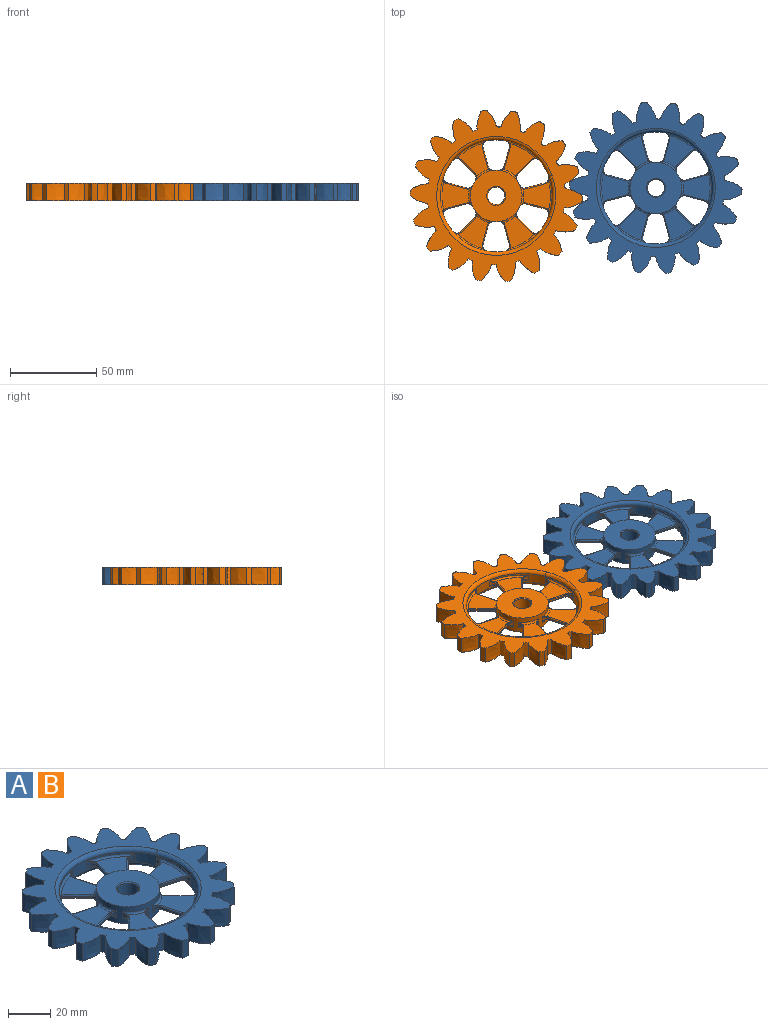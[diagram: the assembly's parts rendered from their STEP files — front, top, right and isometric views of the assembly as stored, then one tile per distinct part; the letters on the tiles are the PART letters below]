
ASSEMBLY  parts=2 mates=1
PART A: 303 faces, bbox 100x99.4x10 mm
  f0: plane 8.2x8.2mm, normal (0.71,-0.71,0), area 11.6mm2, adj f1,f5,f163,f208
  f1: cylinder r=3mm len=4mm, axis (0,0,1), area 8.2mm2, adj f0,f115,f161,f162,f209,f210
  f2: cylinder r=3mm len=4mm, axis (0,0,1), area 8.2mm2, adj f3,f115,f171,f172,f224,f225
  f3: plane 11.2x3mm, normal (-0.26,0.97,0), area 11.6mm2, adj f2,f4,f173,f223
  f4: cylinder r=3mm len=4mm, axis (0,0,1), area 9.6mm2, adj f3,f116,f174,f175,f221,f222
  f5: cylinder r=3mm len=4.45mm, axis (0,0,1), area 9.6mm2, adj f0,f116,f164,f165,f206,f207
  f6: plane 11.2x3mm, normal (-0.26,-0.97,0), area 11.6mm2, adj f7,f11,f168,f218
  f7: cylinder r=3mm len=4mm, axis (0,0,1), area 8.2mm2, adj f6,f115,f166,f167,f219,f220
  f8: cylinder r=3mm len=4mm, axis (0,0,1), area 8.2mm2, adj f9,f115,f256,f257,f269,f270
  f9: plane 8.2x8.2mm, normal (0.71,0.71,0), area 11.6mm2, adj f8,f10,f258,f268
  f10: cylinder r=3mm len=4.45mm, axis (0,0,1), area 9.6mm2, adj f9,f116,f259,f260,f266,f267
  f11: cylinder r=3mm len=4mm, axis (0,0,1), area 9.6mm2, adj f6,f116,f169,f170,f216,f217
  f12: plane 11.2x3mm, normal (-0.97,-0.26,0), area 11.6mm2, adj f13,f17,f263,f273
  f13: cylinder r=3mm len=4mm, axis (0,0,1), area 8.2mm2, adj f12,f115,f264,f265,f271,f272
  f14: cylinder r=3mm len=4mm, axis (0,0,1), area 8.2mm2, adj f15,f115,f181,f182,f254,f255
  f15: plane 11.2x3mm, normal (0.97,-0.26,0), area 11.6mm2, adj f14,f16,f183,f253
  f16: cylinder r=3mm len=4mm, axis (0,0,1), area 9.6mm2, adj f15,f116,f184,f185,f251,f252
  f17: cylinder r=3mm len=4mm, axis (0,0,1), area 9.6mm2, adj f12,f116,f261,f262,f274,f275
  f18: plane 8.2x8.2mm, normal (-0.71,0.71,0), area 11.6mm2, adj f19,f23,f203,f248
  f19: cylinder r=3mm len=4mm, axis (0,0,1), area 8.2mm2, adj f18,f115,f204,f205,f249,f250
  f20: cylinder r=3mm len=4mm, axis (0,0,1), area 8.2mm2, adj f21,f115,f199,f200,f244,f245
  f21: plane 11.2x3mm, normal (0.26,-0.97,0), area 11.6mm2, adj f20,f22,f198,f243
  f22: cylinder r=3mm len=4mm, axis (0,0,1), area 9.6mm2, adj f21,f116,f196,f197,f241,f242
  f23: cylinder r=3mm len=4.45mm, axis (0,0,1), area 9.6mm2, adj f18,f116,f201,f202,f246,f247
  f24: plane 11.2x3mm, normal (0.26,0.97,0), area 11.6mm2, adj f25,f29,f193,f238
  f25: cylinder r=3mm len=4mm, axis (0,0,1), area 8.2mm2, adj f24,f115,f194,f195,f239,f240
  f26: cylinder r=3mm len=4mm, axis (0,0,1), area 8.2mm2, adj f27,f115,f189,f190,f234,f235
  f27: plane 8.2x8.2mm, normal (-0.71,-0.71,0), area 11.6mm2, adj f26,f28,f188,f233
  f28: cylinder r=3mm len=4.45mm, axis (0,0,1), area 9.6mm2, adj f27,f116,f186,f187,f231,f232
  f29: cylinder r=3mm len=4mm, axis (0,0,1), area 9.6mm2, adj f24,f116,f191,f192,f236,f237
  f30: plane 11.2x3mm, normal (0.97,0.26,0), area 11.6mm2, adj f31,f35,f178,f228
  f31: cylinder r=3mm len=4mm, axis (0,0,1), area 8.2mm2, adj f30,f115,f176,f177,f229,f230
  f32: cylinder r=3mm len=4mm, axis (0,0,1), area 8.2mm2, adj f33,f115,f214,f215,f279,f280
  f33: plane 11.2x3mm, normal (-0.97,0.26,0), area 11.6mm2, adj f32,f34,f213,f278
  f34: cylinder r=3mm len=4mm, axis (0,0,1), area 9.6mm2, adj f33,f116,f211,f212,f276,f277
  f35: cylinder r=3mm len=4mm, axis (0,0,1), area 9.6mm2, adj f30,f116,f179,f180,f226,f227
  f36: plane 30x30mm, normal (0,0,-1), area 611.8mm2, adj f113,f115,f132
  f37: plane 99.99x99.35mm, normal (0,0,-1), area 2808.6mm2, adj f40,f41,f42,f43,f44,f45,f46,f47
  f38: plane 30x30mm, normal (0,0,1), area 611.8mm2, adj f114,f115,f124
  f39: plane 99.99x99.35mm, normal (0,0,1), area 2808.6mm2, adj f40,f41,f42,f43,f44,f45,f46,f47
  f40: cylinder r=50mm len=10mm, axis (0,0,-1), area 32.4mm2, adj f37,f39,f63,f109
  f41: cylinder r=50mm len=10mm, axis (0,0,-1), area 32.4mm2, adj f37,f39,f66,f106
  f42: cylinder r=50mm len=10mm, axis (0,0,-1), area 32.4mm2, adj f37,f39,f102,f103
  f43: cylinder r=50mm len=10mm, axis (0,0,-1), area 32.4mm2, adj f37,f39,f100,f108
  f44: cylinder r=50mm len=10mm, axis (0,0,-1), area 32.4mm2, adj f37,f39,f97,f111
  f45: cylinder r=50mm len=10mm, axis (0,0,-1), area 32.4mm2, adj f37,f39,f94,f99
  f46: cylinder r=50mm len=10mm, axis (0,0,-1), area 17.2mm2, adj f37,f39,f298,f302
  f47: cylinder r=50mm len=10mm, axis (0,0,-1), area 17.2mm2, adj f37,f39,f281,f299
  f48: cylinder r=50mm len=10mm, axis (0,0,-1), area 17.2mm2, adj f37,f39,f294,f296
  f49: cylinder r=50mm len=10mm, axis (0,0,-1), area 17.2mm2, adj f37,f39,f286,f288
  f50: cylinder r=50mm len=10mm, axis (0,0,-1), area 17.2mm2, adj f37,f39,f282,f284
  f51: cylinder r=50mm len=10mm, axis (0,0,-1), area 32.4mm2, adj f37,f39,f75,f76
  f52: cylinder r=50mm len=10mm, axis (0,0,-1), area 32.4mm2, adj f37,f39,f73,f81
  f53: cylinder r=50mm len=10mm, axis (0,0,-1), area 32.4mm2, adj f37,f39,f70,f78
  f54: cylinder r=50mm len=10mm, axis (0,0,-1), area 32.4mm2, adj f37,f39,f67,f72
  f55: cylinder r=50mm len=10mm, axis (0,0,-1), area 32.4mm2, adj f37,f39,f64,f69
  f56: cylinder r=50mm len=10mm, axis (0,0,-1), area 32.4mm2, adj f37,f39,f61,f105
  f57: cylinder r=50mm len=10mm, axis (0,0,-1), area 17.2mm2, adj f37,f39,f290,f292
  f58: extruded ~10x8.03mm, area 93.6mm2, adj f37,f39,f289,f290
  f59: cylinder r=40mm len=10mm, axis (0,0,1), area 3.4mm2, adj f37,f39,f287,f289
  f60: extruded ~10x9.25mm, area 93.6mm2, adj f37,f39,f287,f288
  f61: extruded ~10.49x10mm, area 112.7mm2, adj f37,f39,f56,f62
  f62: cylinder r=40mm len=10mm, axis (0,0,1), area 27.9mm2, adj f37,f39,f61,f63
  f63: extruded ~10x8.13mm, area 112.7mm2, adj f37,f39,f40,f62
  f64: extruded ~10.96x10mm, area 112.7mm2, adj f37,f39,f55,f65
  f65: cylinder r=40mm len=10mm, axis (0,0,1), area 27.9mm2, adj f37,f39,f64,f66
  f66: extruded ~10x8.84mm, area 112.7mm2, adj f37,f39,f41,f65
  f67: extruded ~10x9.71mm, area 112.7mm2, adj f37,f39,f54,f68
  f68: cylinder r=40mm len=10mm, axis (0,0,1), area 27.9mm2, adj f37,f39,f67,f69
  f69: extruded ~10x9.32mm, area 112.7mm2, adj f37,f39,f55,f68
  f70: extruded ~10x8.35mm, area 112.7mm2, adj f37,f39,f53,f71
  f71: cylinder r=40mm len=10mm, axis (0,0,1), area 27.9mm2, adj f37,f39,f70,f72
  f72: extruded ~10.81x10mm, area 112.7mm2, adj f37,f39,f54,f71
  f73: extruded ~11.09x10mm, area 112.7mm2, adj f37,f39,f52,f74
  f74: cylinder r=40mm len=10mm, axis (0,0,1), area 27.9mm2, adj f37,f39,f73,f75
  f75: extruded ~10x9.87mm, area 112.7mm2, adj f37,f39,f51,f74
  f76: extruded ~10.34x10mm, area 112.7mm2, adj f37,f39,f51,f77
  f77: cylinder r=40mm len=10mm, axis (0,0,1), area 27.9mm2, adj f37,f39,f76,f78
  f78: extruded ~11x10mm, area 112.7mm2, adj f37,f39,f53,f77
  f79: extruded ~10x9.85mm, area 105mm2, adj f37,f39,f80,f282
  f80: cylinder r=40mm len=10mm, axis (0,0,1), area 27.9mm2, adj f37,f39,f79,f81
  f81: extruded ~10x8.13mm, area 112.7mm2, adj f37,f39,f52,f80
  f82: extruded ~10x7.1mm, area 93.6mm2, adj f37,f39,f285,f286
  f83: cylinder r=40mm len=10mm, axis (0,0,1), area 3.4mm2, adj f37,f39,f283,f285
  f84: extruded ~10x8.47mm, area 93.6mm2, adj f37,f39,f283,f284
  f85: extruded ~10x9.13mm, area 93.6mm2, adj f37,f39,f293,f294
  f86: cylinder r=40mm len=10mm, axis (0,0,1), area 3.4mm2, adj f37,f39,f291,f293
  f87: extruded ~10x8.92mm, area 93.6mm2, adj f37,f39,f291,f292
  f88: extruded ~10x8.03mm, area 93.6mm2, adj f37,f39,f299,f300
  f89: cylinder r=40mm len=10mm, axis (0,0,1), area 3.4mm2, adj f37,f39,f300,f301
  f90: extruded ~10x7.69mm, area 93.6mm2, adj f37,f39,f301,f302
  f91: extruded ~10x9.13mm, area 93.6mm2, adj f37,f39,f297,f298
  f92: cylinder r=40mm len=10mm, axis (0,0,1), area 3.4mm2, adj f37,f39,f295,f297
  f93: extruded ~10x7.5mm, area 93.6mm2, adj f37,f39,f295,f296
  f94: extruded ~10x8.35mm, area 112.7mm2, adj f37,f39,f45,f95
  f95: cylinder r=40mm len=10mm, axis (0,0,1), area 27.9mm2, adj f37,f39,f94,f96
  f96: extruded ~10.13x10mm, area 105mm2, adj f37,f39,f95,f281
  f97: extruded ~10.34x10mm, area 112.7mm2, adj f37,f39,f44,f98
  f98: cylinder r=40mm len=10mm, axis (0,0,1), area 27.9mm2, adj f37,f39,f97,f99
  f99: extruded ~11x10mm, area 112.7mm2, adj f37,f39,f45,f98
  f100: extruded ~10x9.49mm, area 112.7mm2, adj f37,f39,f43,f101
  f101: cylinder r=40mm len=10mm, axis (0,0,1), area 27.9mm2, adj f37,f39,f100,f102
  f102: extruded ~11.08x10mm, area 112.7mm2, adj f37,f39,f42,f101
  f103: extruded ~10x8.64mm, area 112.7mm2, adj f37,f39,f42,f104
  f104: cylinder r=40mm len=10mm, axis (0,0,1), area 27.9mm2, adj f37,f39,f103,f105
  f105: extruded ~10.22x10mm, area 112.7mm2, adj f37,f39,f56,f104
  f106: extruded ~10.88x10mm, area 112.7mm2, adj f37,f39,f41,f107
  f107: cylinder r=40mm len=10mm, axis (0,0,1), area 27.9mm2, adj f37,f39,f106,f108
  f108: extruded ~10.6x10mm, area 112.7mm2, adj f37,f39,f43,f107
  f109: extruded ~11.09x10mm, area 112.7mm2, adj f37,f39,f40,f110
  f110: cylinder r=40mm len=10mm, axis (0,0,1), area 27.9mm2, adj f37,f39,f109,f111
  f111: extruded ~10x9.87mm, area 112.7mm2, adj f37,f39,f44,f110
  f112: cylinder r=5mm len=10mm, axis (0,0,1), area 282.7mm2, adj f113,f114
  f113: cone r=5.5mm half-angle=45deg, axis (0,0,-1), area 23.3mm2, adj f36,f112
  f114: cone r=5mm half-angle=45deg, axis (0,0,1), area 23.3mm2, adj f38,f112
  f115: cylinder r=15mm len=30mm, axis (0,0,1), area 556.2mm2, adj f1,f2,f7,f8,f13,f14,f19,f20
  f116: cylinder r=32.5mm len=65mm, axis (0,0,1), area 610.6mm2, adj f4,f5,f10,f11,f16,f17,f22,f23
  f117: plane 19.15x18.27mm, normal (0,0,1), area 178.8mm2, adj f152,f156,f177,f178,f179,f187,f188,f189
  f118: plane 19.15x18.27mm, normal (0,0,1), area 178.8mm2, adj f159,f160,f162,f163,f164,f277,f278,f279
  f119: plane 16.77x16.04mm, normal (0,0,1), area 178.8mm2, adj f151,f155,f192,f193,f194,f197,f198,f199
  f120: plane 19.15x18.27mm, normal (0,0,1), area 178.8mm2, adj f150,f154,f182,f183,f184,f202,f203,f204
  f121: plane 19.15x18.27mm, normal (0,0,1), area 178.8mm2, adj f149,f153,f267,f268,f269,f272,f273,f274
  f122: plane 16.78x16.04mm, normal (0,0,1), area 178.8mm2, adj f157,f158,f167,f168,f169,f172,f173,f174
  f123: extruded ~23.12x2.13mm, area 23.6mm2, adj f116,f136,f157
  f124: extruded ~12.49x3mm, area 38.6mm2, adj f38,f115,f158
  f125: plane 19.15x18.27mm, normal (0,0,-1), area 178.8mm2, adj f140,f144,f227,f228,f229,f232,f233,f234
  f126: plane 19.15x18.27mm, normal (0,0,-1), area 178.8mm2, adj f147,f148,f207,f208,f209,f212,f213,f214
  f127: plane 16.77x16.04mm, normal (0,0,-1), area 178.8mm2, adj f139,f143,f237,f238,f239,f242,f243,f244
  f128: plane 19.15x18.27mm, normal (0,0,-1), area 178.8mm2, adj f138,f142,f247,f248,f249,f252,f253,f254
  f129: plane 19.15x18.27mm, normal (0,0,-1), area 178.8mm2, adj f137,f141,f257,f258,f259,f262,f263,f264
  f130: plane 16.78x16.04mm, normal (0,0,-1), area 178.8mm2, adj f145,f146,f217,f218,f219,f222,f223,f224
  f131: extruded ~23.12x2.13mm, area 23.6mm2, adj f116,f134,f145
  f132: extruded ~12.49x3mm, area 38.6mm2, adj f36,f115,f146
  f133: torus R=34.5mm, axis (0,0,1), area 579.9mm2, adj f37,f116,f134
  f134: bspline ~32.37x5.62mm, area 75.9mm2, adj f37,f131,f133
  f135: torus R=34.5mm, axis (0,0,1), area 579.9mm2, adj f39,f116,f136
  f136: bspline ~32.37x5.62mm, area 75.9mm2, adj f39,f123,f135
  f137: torus R=31.5mm, axis (0,0,-1), area 32mm2, adj f116,f129,f260,f261
  f138: torus R=31.5mm, axis (0,0,-1), area 32mm2, adj f116,f128,f246,f251
  f139: torus R=31.5mm, axis (0,0,-1), area 32mm2, adj f116,f127,f236,f241
  f140: torus R=31.5mm, axis (0,0,-1), area 32mm2, adj f116,f125,f226,f231
  f141: torus R=16mm, axis (0,0,-1), area 16.6mm2, adj f115,f129,f256,f265
  f142: torus R=16mm, axis (0,0,-1), area 16.6mm2, adj f115,f128,f250,f255
  f143: torus R=16mm, axis (0,0,-1), area 16.6mm2, adj f115,f127,f240,f245
  f144: torus R=16mm, axis (0,0,-1), area 16.6mm2, adj f115,f125,f230,f235
  f145: bspline ~27.91x4.74mm, area 32mm2, adj f130,f131,f216,f221
  f146: bspline ~13.79x2.51mm, area 16.6mm2, adj f130,f132,f220,f225
  f147: torus R=16mm, axis (0,0,-1), area 16.6mm2, adj f115,f126,f210,f215
  f148: torus R=31.5mm, axis (0,0,-1), area 32mm2, adj f116,f126,f206,f211
  f149: torus R=31.5mm, axis (0,0,1), area 32mm2, adj f116,f121,f266,f275
  f150: torus R=31.5mm, axis (0,0,1), area 32mm2, adj f116,f120,f185,f201
  f151: torus R=31.5mm, axis (0,0,1), area 32mm2, adj f116,f119,f191,f196
  f152: torus R=31.5mm, axis (0,0,1), area 32mm2, adj f116,f117,f180,f186
  f153: torus R=16mm, axis (0,0,1), area 16.6mm2, adj f115,f121,f270,f271
  f154: torus R=16mm, axis (0,0,1), area 16.6mm2, adj f115,f120,f181,f205
  f155: torus R=16mm, axis (0,0,1), area 16.6mm2, adj f115,f119,f195,f200
  f156: torus R=16mm, axis (0,0,1), area 16.6mm2, adj f115,f117,f176,f190
  f157: bspline ~27.91x4.74mm, area 32mm2, adj f122,f123,f170,f175
  f158: bspline ~14.11x2.58mm, area 16.6mm2, adj f122,f124,f166,f171
  f159: torus R=16mm, axis (0,0,1), area 16.6mm2, adj f115,f118,f161,f280
  f160: torus R=31.5mm, axis (0,0,1), area 32mm2, adj f116,f118,f165,f276
  f161: bspline ~2.9x1.5mm, area 0.8mm2, adj f1,f159,f162
  f162: torus R=3.5mm, axis (0,0,1), area 1.3mm2, adj f1,f118,f161,f163
  f163: cylinder r=0.5mm len=8.56mm, axis (-0.71,-0.71,0), area 9.1mm2, adj f0,f118,f162,f164
  f164: torus R=3.5mm, axis (0,0,1), area 1.7mm2, adj f5,f118,f163,f165
  f165: bspline ~3.06x1.59mm, area 0.9mm2, adj f5,f160,f164
  f166: bspline ~2.24x2.23mm, area 0.8mm2, adj f7,f158,f167
  f167: torus R=3.5mm, axis (0,0,1), area 1.3mm2, adj f7,f122,f166,f168
  f168: cylinder r=0.5mm len=11.33mm, axis (-0.97,0.26,0), area 9.1mm2, adj f6,f122,f167,f169
  f169: torus R=3.5mm, axis (0,0,1), area 1.7mm2, adj f11,f122,f168,f170
  f170: bspline ~3.44x1.5mm, area 0.9mm2, adj f11,f157,f169
  f171: bspline ~2.24x2.23mm, area 0.8mm2, adj f2,f158,f172
  f172: torus R=3.5mm, axis (0,0,1), area 1.3mm2, adj f2,f122,f171,f173
  f173: cylinder r=0.5mm len=11.33mm, axis (0.97,0.26,0), area 9.1mm2, adj f3,f122,f172,f174
  f174: torus R=3.5mm, axis (0,0,1), area 1.7mm2, adj f4,f122,f173,f175
  f175: bspline ~3.44x1.5mm, area 0.9mm2, adj f4,f157,f174
  f176: bspline ~2.96x1.5mm, area 0.8mm2, adj f31,f156,f177
  f177: torus R=3.5mm, axis (0,0,1), area 1.3mm2, adj f31,f117,f176,f178
  f178: cylinder r=0.5mm len=11.33mm, axis (0.26,-0.97,0), area 9.1mm2, adj f30,f117,f177,f179
  f179: torus R=3.5mm, axis (0,0,1), area 1.7mm2, adj f35,f117,f178,f180
  f180: bspline ~2.75x1.79mm, area 0.9mm2, adj f35,f152,f179
  f181: bspline ~2.96x1.5mm, area 0.8mm2, adj f14,f154,f182
  f182: torus R=3.5mm, axis (0,0,1), area 1.3mm2, adj f14,f120,f181,f183
  f183: cylinder r=0.5mm len=11.33mm, axis (-0.26,-0.97,0), area 9.1mm2, adj f15,f120,f182,f184
  f184: torus R=3.5mm, axis (0,0,1), area 1.7mm2, adj f16,f120,f183,f185
  f185: bspline ~2.9x2.1mm, area 0.9mm2, adj f16,f150,f184
  f186: bspline ~3.06x1.59mm, area 0.9mm2, adj f28,f152,f187
  f187: torus R=3.5mm, axis (0,0,1), area 1.7mm2, adj f28,f117,f186,f188
  f188: cylinder r=0.5mm len=8.56mm, axis (-0.71,0.71,0), area 9.1mm2, adj f27,f117,f187,f189
  f189: torus R=3.5mm, axis (0,0,1), area 1.3mm2, adj f26,f117,f188,f190
  f190: bspline ~2.9x1.5mm, area 0.8mm2, adj f26,f156,f189
  f191: bspline ~3.44x1.5mm, area 0.9mm2, adj f29,f151,f192
  f192: torus R=3.5mm, axis (0,0,1), area 1.7mm2, adj f29,f119,f191,f193
  f193: cylinder r=0.5mm len=11.33mm, axis (0.97,-0.26,0), area 9.1mm2, adj f24,f119,f192,f194
  f194: torus R=3.5mm, axis (0,0,1), area 1.3mm2, adj f25,f119,f193,f195
  f195: bspline ~2.24x2.23mm, area 0.8mm2, adj f25,f155,f194
  f196: bspline ~3.44x1.5mm, area 0.9mm2, adj f22,f151,f197
  f197: torus R=3.5mm, axis (0,0,1), area 1.7mm2, adj f22,f119,f196,f198
  f198: cylinder r=0.5mm len=11.33mm, axis (-0.97,-0.26,0), area 9.1mm2, adj f21,f119,f197,f199
  f199: torus R=3.5mm, axis (0,0,1), area 1.3mm2, adj f20,f119,f198,f200
  f200: bspline ~2.24x2.23mm, area 0.8mm2, adj f20,f155,f199
  f201: bspline ~3.06x1.59mm, area 0.9mm2, adj f23,f150,f202
  f202: torus R=3.5mm, axis (0,0,1), area 1.7mm2, adj f23,f120,f201,f203
  f203: cylinder r=0.5mm len=8.56mm, axis (0.71,0.71,0), area 9.1mm2, adj f18,f120,f202,f204
  f204: torus R=3.5mm, axis (0,0,1), area 1.3mm2, adj f19,f120,f203,f205
  f205: bspline ~2.9x1.5mm, area 0.8mm2, adj f19,f154,f204
  f206: bspline ~3.06x1.59mm, area 0.9mm2, adj f5,f148,f207
  f207: torus R=3.5mm, axis (0,0,-1), area 1.7mm2, adj f5,f126,f206,f208
  f208: cylinder r=0.5mm len=8.56mm, axis (0.71,0.71,0), area 9.1mm2, adj f0,f126,f207,f209
  f209: torus R=3.5mm, axis (0,0,-1), area 1.3mm2, adj f1,f126,f208,f210
  f210: bspline ~2.9x1.5mm, area 0.8mm2, adj f1,f147,f209
  f211: bspline ~2.9x2.1mm, area 0.9mm2, adj f34,f148,f212
  f212: torus R=3.5mm, axis (0,0,-1), area 1.7mm2, adj f34,f126,f211,f213
  f213: cylinder r=0.5mm len=11.33mm, axis (-0.26,-0.97,0), area 9.1mm2, adj f33,f126,f212,f214
  f214: torus R=3.5mm, axis (0,0,-1), area 1.3mm2, adj f32,f126,f213,f215
  f215: bspline ~2.96x1.5mm, area 0.8mm2, adj f32,f147,f214
  f216: bspline ~3.44x1.5mm, area 0.9mm2, adj f11,f145,f217
  f217: torus R=3.5mm, axis (0,0,-1), area 1.7mm2, adj f11,f130,f216,f218
  f218: cylinder r=0.5mm len=11.33mm, axis (0.97,-0.26,0), area 9.1mm2, adj f6,f130,f217,f219
  f219: torus R=3.5mm, axis (0,0,-1), area 1.3mm2, adj f7,f130,f218,f220
  f220: bspline ~2.24x2.23mm, area 0.8mm2, adj f7,f146,f219
  f221: bspline ~3.44x1.5mm, area 0.9mm2, adj f4,f145,f222
  f222: torus R=3.5mm, axis (0,0,-1), area 1.7mm2, adj f4,f130,f221,f223
  f223: cylinder r=0.5mm len=11.33mm, axis (-0.97,-0.26,0), area 9.1mm2, adj f3,f130,f222,f224
  f224: torus R=3.5mm, axis (0,0,-1), area 1.3mm2, adj f2,f130,f223,f225
  f225: bspline ~2.24x2.23mm, area 0.8mm2, adj f2,f146,f224
  f226: bspline ~2.9x2.1mm, area 0.9mm2, adj f35,f140,f227
  f227: torus R=3.5mm, axis (0,0,-1), area 1.7mm2, adj f35,f125,f226,f228
  f228: cylinder r=0.5mm len=11.33mm, axis (-0.26,0.97,0), area 9.1mm2, adj f30,f125,f227,f229
  f229: torus R=3.5mm, axis (0,0,-1), area 1.3mm2, adj f31,f125,f228,f230
  f230: bspline ~2.96x1.5mm, area 0.8mm2, adj f31,f144,f229
  f231: bspline ~3.06x1.59mm, area 0.9mm2, adj f28,f140,f232
  f232: torus R=3.5mm, axis (0,0,-1), area 1.7mm2, adj f28,f125,f231,f233
  f233: cylinder r=0.5mm len=8.56mm, axis (0.71,-0.71,0), area 9.1mm2, adj f27,f125,f232,f234
  f234: torus R=3.5mm, axis (0,0,-1), area 1.3mm2, adj f26,f125,f233,f235
  f235: bspline ~2.9x1.5mm, area 0.8mm2, adj f26,f144,f234
  f236: bspline ~3.44x1.5mm, area 0.9mm2, adj f29,f139,f237
  f237: torus R=3.5mm, axis (0,0,-1), area 1.7mm2, adj f29,f127,f236,f238
  f238: cylinder r=0.5mm len=11.33mm, axis (-0.97,0.26,0), area 9.1mm2, adj f24,f127,f237,f239
  f239: torus R=3.5mm, axis (0,0,-1), area 1.3mm2, adj f25,f127,f238,f240
  f240: bspline ~2.24x2.23mm, area 0.8mm2, adj f25,f143,f239
  f241: bspline ~3.44x1.5mm, area 0.9mm2, adj f22,f139,f242
  f242: torus R=3.5mm, axis (0,0,-1), area 1.7mm2, adj f22,f127,f241,f243
  f243: cylinder r=0.5mm len=11.33mm, axis (0.97,0.26,0), area 9.1mm2, adj f21,f127,f242,f244
  f244: torus R=3.5mm, axis (0,0,-1), area 1.3mm2, adj f20,f127,f243,f245
  f245: bspline ~2.24x2.23mm, area 0.8mm2, adj f20,f143,f244
  f246: bspline ~3.06x1.59mm, area 0.9mm2, adj f23,f138,f247
  f247: torus R=3.5mm, axis (0,0,-1), area 1.7mm2, adj f23,f128,f246,f248
  f248: cylinder r=0.5mm len=8.56mm, axis (-0.71,-0.71,0), area 9.1mm2, adj f18,f128,f247,f249
  f249: torus R=3.5mm, axis (0,0,-1), area 1.3mm2, adj f19,f128,f248,f250
  f250: bspline ~2.9x1.5mm, area 0.8mm2, adj f19,f142,f249
  f251: bspline ~2.9x2.1mm, area 0.9mm2, adj f16,f138,f252
  f252: torus R=3.5mm, axis (0,0,-1), area 1.7mm2, adj f16,f128,f251,f253
  f253: cylinder r=0.5mm len=11.33mm, axis (0.26,0.97,0), area 9.1mm2, adj f15,f128,f252,f254
  f254: torus R=3.5mm, axis (0,0,-1), area 1.3mm2, adj f14,f128,f253,f255
  f255: bspline ~2.96x1.5mm, area 0.8mm2, adj f14,f142,f254
  f256: bspline ~2.9x1.5mm, area 0.8mm2, adj f8,f141,f257
  f257: torus R=3.5mm, axis (0,0,-1), area 1.3mm2, adj f8,f129,f256,f258
  f258: cylinder r=0.5mm len=8.56mm, axis (-0.71,0.71,0), area 9.1mm2, adj f9,f129,f257,f259
  f259: torus R=3.5mm, axis (0,0,-1), area 1.7mm2, adj f10,f129,f258,f260
  f260: bspline ~2.76x1.58mm, area 0.9mm2, adj f10,f137,f259
  f261: bspline ~2.9x2.1mm, area 0.9mm2, adj f17,f137,f262
  f262: torus R=3.5mm, axis (0,0,-1), area 1.7mm2, adj f17,f129,f261,f263
  f263: cylinder r=0.5mm len=11.33mm, axis (0.26,-0.97,0), area 9.1mm2, adj f12,f129,f262,f264
  f264: torus R=3.5mm, axis (0,0,-1), area 1.3mm2, adj f13,f129,f263,f265
  f265: bspline ~2.96x1.5mm, area 0.8mm2, adj f13,f141,f264
  f266: bspline ~3.06x1.59mm, area 0.9mm2, adj f10,f149,f267
  f267: torus R=3.5mm, axis (0,0,1), area 1.7mm2, adj f10,f121,f266,f268
  f268: cylinder r=0.5mm len=8.56mm, axis (0.71,-0.71,0), area 9.1mm2, adj f9,f121,f267,f269
  f269: torus R=3.5mm, axis (0,0,1), area 1.3mm2, adj f8,f121,f268,f270
  f270: bspline ~2.9x1.5mm, area 0.8mm2, adj f8,f153,f269
  f271: bspline ~2.96x1.5mm, area 0.8mm2, adj f13,f153,f272
  f272: torus R=3.5mm, axis (0,0,1), area 1.3mm2, adj f13,f121,f271,f273
  f273: cylinder r=0.5mm len=11.33mm, axis (-0.26,0.97,0), area 9.1mm2, adj f12,f121,f272,f274
  f274: torus R=3.5mm, axis (0,0,1), area 1.7mm2, adj f17,f121,f273,f275
  f275: bspline ~2.75x1.79mm, area 0.9mm2, adj f17,f149,f274
  f276: bspline ~2.9x2.1mm, area 0.9mm2, adj f34,f160,f277
  f277: torus R=3.5mm, axis (0,0,1), area 1.7mm2, adj f34,f118,f276,f278
  f278: cylinder r=0.5mm len=11.33mm, axis (0.26,0.97,0), area 9.1mm2, adj f33,f118,f277,f279
  f279: torus R=3.5mm, axis (0,0,1), area 1.3mm2, adj f32,f118,f278,f280
  f280: bspline ~2.96x1.5mm, area 0.8mm2, adj f32,f159,f279
  f281: cylinder r=1.5mm len=10mm, axis (0,0,1), area 14.2mm2, adj f37,f39,f47,f96
  f282: cylinder r=1.5mm len=10mm, axis (0,0,1), area 14.2mm2, adj f37,f39,f50,f79
  f283: cylinder r=1.5mm len=10mm, axis (0,0,1), area 19.5mm2, adj f37,f39,f83,f84
  f284: cylinder r=1.5mm len=10mm, axis (0,0,1), area 14.2mm2, adj f37,f39,f50,f84
  f285: cylinder r=1.5mm len=10mm, axis (0,0,1), area 19.5mm2, adj f37,f39,f82,f83
  f286: cylinder r=1.5mm len=10mm, axis (0,0,1), area 14.2mm2, adj f37,f39,f49,f82
  f287: cylinder r=1.5mm len=10mm, axis (0,0,1), area 19.5mm2, adj f37,f39,f59,f60
  f288: cylinder r=1.5mm len=10mm, axis (0,0,1), area 14.2mm2, adj f37,f39,f49,f60
  f289: cylinder r=1.5mm len=10mm, axis (0,0,1), area 19.5mm2, adj f37,f39,f58,f59
  f290: cylinder r=1.5mm len=10mm, axis (0,0,1), area 14.2mm2, adj f37,f39,f57,f58
  f291: cylinder r=1.5mm len=10mm, axis (0,0,1), area 19.5mm2, adj f37,f39,f86,f87
  f292: cylinder r=1.5mm len=10mm, axis (0,0,1), area 14.2mm2, adj f37,f39,f57,f87
  f293: cylinder r=1.5mm len=10mm, axis (0,0,1), area 19.5mm2, adj f37,f39,f85,f86
  f294: cylinder r=1.5mm len=10mm, axis (0,0,1), area 14.2mm2, adj f37,f39,f48,f85
  f295: cylinder r=1.5mm len=10mm, axis (0,0,1), area 19.5mm2, adj f37,f39,f92,f93
  f296: cylinder r=1.5mm len=10mm, axis (0,0,1), area 14.2mm2, adj f37,f39,f48,f93
  f297: cylinder r=1.5mm len=10mm, axis (0,0,1), area 19.5mm2, adj f37,f39,f91,f92
  f298: cylinder r=1.5mm len=10mm, axis (0,0,1), area 14.2mm2, adj f37,f39,f46,f91
  f299: cylinder r=1.5mm len=10mm, axis (0,0,1), area 14.2mm2, adj f37,f39,f47,f88
  f300: cylinder r=1.5mm len=10mm, axis (0,0,1), area 19.5mm2, adj f37,f39,f88,f89
  f301: cylinder r=1.5mm len=10mm, axis (0,0,1), area 19.5mm2, adj f37,f39,f89,f90
  f302: cylinder r=1.5mm len=10mm, axis (0,0,1), area 14.2mm2, adj f37,f39,f46,f90
PART B: same geometry as A
PLACE A t=(95.15,3.75,-3.63)mm
PLACE B rot(axis=(0,0,1),0deg) t=(2.53,-0.87,-3.63)mm
MATE planar B.f115 <-> A.f104  axis (0,0,-1) through (2.53,-0.87,-3.63)mm
